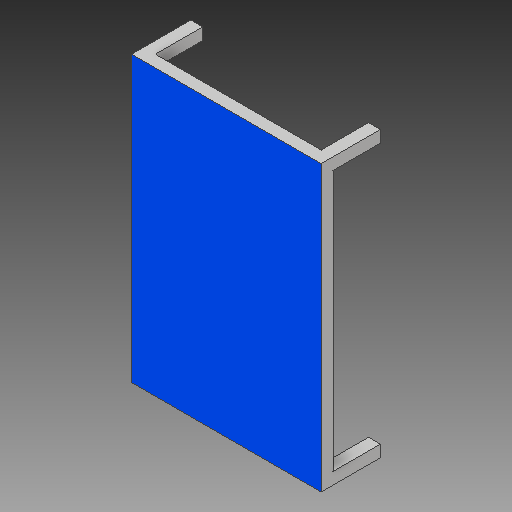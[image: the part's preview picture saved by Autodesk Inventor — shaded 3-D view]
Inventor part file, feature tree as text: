
AUTODESK INVENTOR PART (.ipt)
format: ipt  version: 2018 (Build 220112000, 112)  size: 122,368 bytes
history: native  units: in
note: dims shown in document units (in); Inventor stores cm internally (conversion verified against a paired STEP export)
features: other x3, extrude x2, sketch x2, reference x1
ambient origin geometry x8: Origin, YZ Plane, XZ Plane, XY Plane, X Axis, Y Axis, Z Axis, Center Point
bodies: Solid1 (feature_tree)
feature tree (8):
  extrude  "Extrusion1"  Depth=0.5in
  extrude  "Extrusion2"  Depth=0.5in
  sketch  "Sketch1"  dims[d2=8.0in d3=0.5in]
  reference  "Reference1"
  sketch  "Sketch2"  dims[d4=0.5in d5=0.5in d6=0.5in d7=0.5in d8=2.0in d9=0.0in d10=0.5in d11=0.0in]
  other  "<userpath>\OneDrive\Documents\Inventor\TSA\2018\Animatronics\Tortoise\AssemblyTURTLE.iam"
  other  "AssemblyTURTLE.iam"
  other  "Frame:1"
